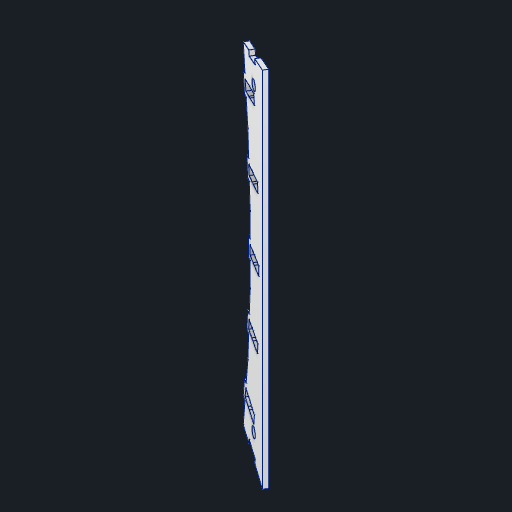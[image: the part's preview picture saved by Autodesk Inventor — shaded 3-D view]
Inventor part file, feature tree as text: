
AUTODESK INVENTOR PART (.ipt)
format: ipt  version: 2023 (Build 270158000, 158)  size: 321,024 bytes
history: native  units: in
note: dims shown in document units (in); Inventor stores cm internally (conversion verified against a paired STEP export)
features: reference x41, other x10, sketch x5, extrude x3, hole x2, plane x1
ambient origin geometry x8: Origin, YZ Plane, XZ Plane, XY Plane, X Axis, Y Axis, Z Axis, Center Point
bodies: Solid1 (feature_tree)
feature tree (62):
  plane  "Work Plane1"
  extrude  "Extrusion1"  Depth=0.125in TaperAngle=0.0deg
  extrude  "Extrusion2"  Depth=0.5in
  hole  "Hole2"  [1 undecoded]
  extrude  "Extrusion3"  Depth=0.25in
  hole  "Hole3"  [1 undecoded]
  sketch  "Sketch1"  dims[d1=1.15in d2=0.125in d3=0.0in]
  reference  "Reference1"
  reference  "Reference2"
  reference  "Reference3"
  reference  "Reference4"
  reference  "Reference5"
  reference  "Reference6"
  reference  "Reference7"
  reference  "Reference8"
  reference  "Reference9"
  reference  "Reference10"
  reference  "Reference11"
  reference  "Reference12"
  reference  "Reference13"
  reference  "Reference14"
  reference  "Reference15"
  reference  "Reference16"
  reference  "Reference17"
  reference  "Reference18"
  reference  "Reference19"
  reference  "Reference20"
  reference  "Reference21"
  reference  "Reference22"
  reference  "Reference23"
  reference  "Reference24"
  reference  "Reference25"
  reference  "Reference26"
  reference  "Reference27"
  reference  "Reference28"
  reference  "Reference29"
  reference  "Reference30"
  reference  "Reference31"
  reference  "Reference32"
  reference  "Reference33"
  reference  "Reference34"
  reference  "Reference35"
  sketch  "Sketch3"  dims[d15=0.125in d16=0.0in d17=0.5in]
  sketch  "Sketch4"  dims[d18=0.5in]
  reference  "Reference43"
  reference  "Reference45"
  sketch  "Sketch5"  dims[d19=0.266in d20=0.75in d21=0.507in d22=0.25in d23=0.5635in d24=0.536in d25=0.0in d26=0.5in]
  sketch  "Sketch6"  dims[d27=0.7216in d28=0.25in d29=0.3608in d30=0.5in d31=0.5in d32=0.5in d33=0.5in d34=0.25in d35=0.7216in d36=0.25in d37=0.7216in d38=0.25in d39=0.7216in d40=0.25in d41=0.7216in d42=0.0in d43=0.0in d44=0.4376in d45=0.4376in d46=0.4376in d47=0.4376in d48=0.4376in d49=0.266in d50=0.75in d51=0.507in d52=0.25in d53=0.5635in d54=0.536in d55=0.0in]
  reference  "Reference52"
  reference  "Reference53"
  reference  "Reference54"
  reference  "Reference55"
  other  "<userpath>\Desktop\WaccaController\Wacca Controller\Touch Segment\Touch Segment.iam"
  other  "Touch Segment.iam"
  other  "Touch Fifth:3"
  other  "Touch Fifth:4"
  other  "Touch Fifth:5"
  other  "Touch Fifth:1"
  other  "Touch Fifth:2"
  other  "SidePlate:2"
  other  "SidePlate:1"
  other  "<userpath>\Desktop\Wacca Controller V2\Touch Segment\Touch Segment.iam"
note: 2 required parameter values undecoded (feature->parameter linkage not recoverable at this tier; creation-order binding heuristic only, values carry confidence <= 0.55)
